# Revit family: T120
name_source: partatom
category: Осветительные приборы
revit_build: Autodesk Revit 2016 (Build: 20161004_0715(x64)
units: mm (PartAtom-declared; Revit-internal decimal feet)

## family parameters
Источник света = Нет
Общий = Нет
Основа = Грань
При загрузке вырезать с полостями = Нет
Размер круглого соединителя = Использовать диаметр
Тип детали = Нормальный
Точка расчета площади = Нет

## types (1)
- T120
    ADSK_Единица измерения = Шт.
    ADSK_Завод-изготовитель = ООО МГК Световые технологии
    ADSK_Классификация нагрузок = Прочее
    ADSK_Количество фаз = 1
    ADSK_Количество фаз числовое = 1
    ADSK_Коэффициент мощности = 0.9
    ADSK_Масса = 0
    ADSK_Наименование = Подвесная профильная система для создания, как декоративных световых эффектов, так и для основного освещения. Корпус изготовлен из экструдированного алюминиевого профиля, окрашенного белой порошковой краской, рассеиватель из PMMA профиля. Торцевые крышки, соединительные элементы и другие аксессуары поставляются отдельно. Внутрь корпуса устанавливается самоклеющаяся светодиодная лента
    ADSK_Напряжение = 230 В
    ADSK_Номинальная мощность = 0 кВт
    ADSK_Полная мощность = 0 кВ·А
    ADSK_Размер_Длина = 1150 мм
    ADSK_Ток = 0 А
    ADSK_Энергоэффективность = 121 лм/Вт
    IP Class = IP20
    URL = http://ltcompany.com
    x = 25 мм
    Блок аварийного питания = Нет
    Выбор_ИС = IES_T120 : T120 1150 LED 3000K (38W)
    Группа модели = Светильники
    Изготовитель = ООО МГК Световые технологии
    Класс Защиты = I
    Класс пожароопасности = Нет
    Климатическая зона = УХЛ4
    Код по классификатору = D5020200
    Корпус = Белый металл
    Область использования = HoReCa/гостиницы/рестораны/кафе, Конференц-залы, Культурно-развлекательные учреждения, Магазины/бутики, Офисно-административные объекты, ТРЦ, Частные интерьеры
    Описание = Подвесная профильная система для создания, как декоративных световых эффектов, так и для основного освещения. Корпус изготовлен из экструдированного алюминиевого профиля, окрашенного белой порошковой краской, рассеиватель из PMMA профиля. Торцевые крышки, соединительные элементы и другие аксессуары поставляются отдельно. Внутрь корпуса устанавливается самоклеющаяся светодиодная лента
    Отметка по умолчанию = 0 мм
    Плафон = Плафон полупрозрачный
    Подвесы.Шаг = 860 мм
    Полная установленная мощность = 0 кВ·А
    Тип ИС = LED
    Тип продукции = Светильник
    Тип светильника = T120 модель : T120 1150 LED 4000K (38W)
